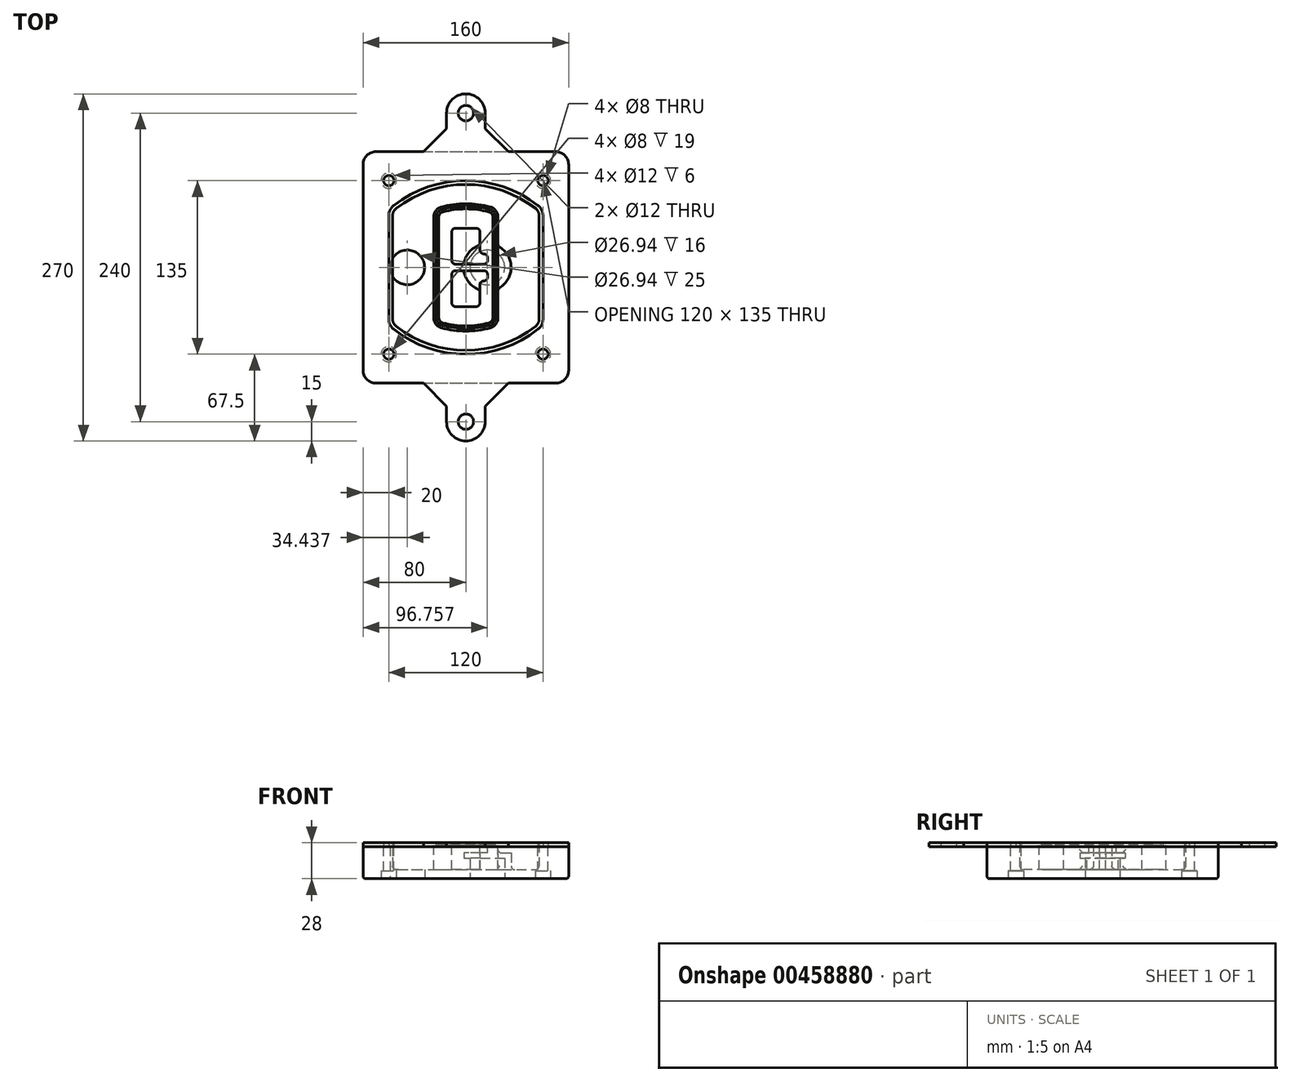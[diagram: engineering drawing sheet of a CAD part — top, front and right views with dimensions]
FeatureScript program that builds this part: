
annotation { "Feature Type Name" : "Feature", "Feature Type Description" : "" }
export const myFeature = defineFeature(function(context is Context, id is Id, definition is map)
    precondition{}
    {
        {
            var Q0;
            Q0=qCreatedBy(makeId("Top.planeOp"),FACE);
            var sketch = newSketch(context, id + "F0", { "sketchPlane" : qUnion([Q0])});
            skPoint(sketch, "E0.rect.middle", {"position": v(0, 0) * mm});
            skLineSegment(sketch, "E1.bottom", {"start": v(-70, -90) * mm, "end": v(70, -90) * mm});
            skLineSegment(sketch, "E1.top", {"start": v(-70, 90) * mm, "end": v(70, 90) * mm});
            skLineSegment(sketch, "E1.left", {"start": v(-80, -80) * mm, "end": v(-80, 80) * mm});
            skLineSegment(sketch, "E1.right", {"start": v(80, -80) * mm, "end": v(80, 80) * mm});
            skLineSegment(sketch, "E2", {"start": v(-80, 90) * mm, "end": v(80, -90) * mm, "construction": true});
            skLineSegment(sketch, "E3", {"start": v(80, 90) * mm, "end": v(-80, -90) * mm, "construction": true});
            skCircle(sketch, "E4", {"center": v(-60, 67.5) * mm, "radius": 4 * mm});
            skCircle(sketch, "E5", {"center": v(60, 67.5) * mm, "radius": 4 * mm});
            skCircle(sketch, "E6", {"center": v(60, -67.5) * mm, "radius": 4 * mm});
            skCircle(sketch, "E7", {"center": v(-60, -67.5) * mm, "radius": 4 * mm});
            skLineSegment(sketch, "E8", {"start": v(-60, 67.5) * mm, "end": v(60, 67.5) * mm, "construction": true});
            skLineSegment(sketch, "E9", {"start": v(60, 67.5) * mm, "end": v(60, -67.5) * mm, "construction": true});
            skLineSegment(sketch, "E10", {"start": v(60, -67.5) * mm, "end": v(-60, -67.5) * mm, "construction": true});
            skLineSegment(sketch, "E11", {"start": v(-60, -67.5) * mm, "end": v(-60, 67.5) * mm, "construction": true});
            skLineSegment(sketch, "E12", {"start": v(-60, 40.3) * mm, "end": v(-60, -40.3) * mm});
            skLineSegment(sketch, "E13", {"start": v(60, 40.3) * mm, "end": v(60, -40.3) * mm});
            skArc(sketch, "E14", {"start": v(56.15, 48.18) * mm, "mid": v(0, 67.5) * mm, "end": v(-56.15, 48.18) * mm});
            skArc(sketch, "E15", {"start": v(-56.15, -48.18) * mm, "mid": v(0, -67.5) * mm, "end": v(56.15, -48.18) * mm});
            skLineSegment(sketch, "E16", {"start": v(-60, 0) * mm, "end": v(60, 0) * mm, "construction": true});
            skPoint(sketch, "E17.visualSharp", {"position": v(-60, -45) * mm});
            skArc(sketch, "E17.filletArc", {"start": v(-60, -40.3) * mm, "mid": v(-58.99, -44.68) * mm, "end": v(-56.15, -48.18) * mm});
            skPoint(sketch, "E18.visualSharp", {"position": v(-60, 45) * mm});
            skArc(sketch, "E18.filletArc", {"start": v(-56.15, 48.18) * mm, "mid": v(-58.99, 44.68) * mm, "end": v(-60, 40.3) * mm});
            skPoint(sketch, "E19.visualSharp", {"position": v(60, 45) * mm});
            skArc(sketch, "E19.filletArc", {"start": v(60, 40.3) * mm, "mid": v(58.99, 44.68) * mm, "end": v(56.15, 48.18) * mm});
            skPoint(sketch, "E20.visualSharp", {"position": v(60, -45) * mm});
            skArc(sketch, "E20.filletArc", {"start": v(56.15, -48.18) * mm, "mid": v(58.99, -44.68) * mm, "end": v(60, -40.3) * mm});
            skPoint(sketch, "E21.visualSharp", {"position": v(-80, 90) * mm});
            skArc(sketch, "E21.filletArc", {"start": v(-70, 90) * mm, "mid": v(-77.07, 87.07) * mm, "end": v(-80, 80) * mm});
            skPoint(sketch, "E22.visualSharp", {"position": v(80, 90) * mm});
            skArc(sketch, "E22.filletArc", {"start": v(80, 80) * mm, "mid": v(77.07, 87.07) * mm, "end": v(70, 90) * mm});
            skPoint(sketch, "E23.visualSharp", {"position": v(80, -90) * mm});
            skArc(sketch, "E23.filletArc", {"start": v(70, -90) * mm, "mid": v(77.07, -87.07) * mm, "end": v(80, -80) * mm});
            skPoint(sketch, "E24.visualSharp", {"position": v(-80, -90) * mm});
            skArc(sketch, "E24.filletArc", {"start": v(-80, -80) * mm, "mid": v(-77.07, -87.07) * mm, "end": v(-70, -90) * mm});
            skArc(sketch, "E25.0", {"start": v(57, 40.3) * mm, "mid": v(56.3, 43.36) * mm, "end": v(54.3, 45.81) * mm});
            skLineSegment(sketch, "E25.1", {"start": v(57, 40.3) * mm, "end": v(57, -40.3) * mm});
            skArc(sketch, "E25.2", {"start": v(54.3, -45.81) * mm, "mid": v(56.3, -43.36) * mm, "end": v(57, -40.3) * mm});
            skArc(sketch, "E25.3", {"start": v(-54.3, -45.81) * mm, "mid": v(0, -64.5) * mm, "end": v(54.3, -45.81) * mm});
            skArc(sketch, "E25.4", {"start": v(-57, -40.3) * mm, "mid": v(-56.3, -43.36) * mm, "end": v(-54.3, -45.81) * mm});
            skArc(sketch, "E25.5", {"start": v(54.3, 45.81) * mm, "mid": v(0, 64.5) * mm, "end": v(-54.3, 45.81) * mm});
            skLineSegment(sketch, "E25.6", {"start": v(-57, 40.3) * mm, "end": v(-57, -40.3) * mm});
            skArc(sketch, "E25.7", {"start": v(-54.3, 45.81) * mm, "mid": v(-56.3, 43.36) * mm, "end": v(-57, 40.3) * mm});
            skArc(sketch, "E26.0", {"start": v(-58.62, 51.33) * mm, "mid": v(-62.58, 46.43) * mm, "end": v(-64, 40.3) * mm});
            skArc(sketch, "E26.1", {"start": v(58.62, 51.33) * mm, "mid": v(0, 71.5) * mm, "end": v(-58.62, 51.33) * mm});
            skArc(sketch, "E26.2", {"start": v(64, 40.3) * mm, "mid": v(62.58, 46.43) * mm, "end": v(58.62, 51.33) * mm});
            skLineSegment(sketch, "E26.3", {"start": v(64, 40.3) * mm, "end": v(64, -40.3) * mm});
            skArc(sketch, "E26.4", {"start": v(58.62, -51.33) * mm, "mid": v(62.58, -46.43) * mm, "end": v(64, -40.3) * mm});
            skLineSegment(sketch, "E26.5", {"start": v(-64, 40.3) * mm, "end": v(-64, -40.3) * mm});
            skArc(sketch, "E26.6", {"start": v(-58.62, -51.33) * mm, "mid": v(0, -71.5) * mm, "end": v(58.62, -51.33) * mm});
            skArc(sketch, "E26.7", {"start": v(-64, -40.3) * mm, "mid": v(-62.58, -46.43) * mm, "end": v(-58.62, -51.33) * mm});
            skSolve(sketch);
        }
        {
            var Q0;
            Q0=makeQuery(id+"F0.imprint","IMPRINT",FACE,{"disambiguationData":[TD([[makeQuery(id+"F0.imprint","IMPRINT",EDGE,{"derivedFrom":sQuery(id+"F0.wireOp",EDGE,"E1.bottom")}),1.0]])]});
            var Q1;
            Q1=makeQuery(id+"F0.imprint","IMPRINT",FACE,{"disambiguationData":[TD([[makeQuery(id+"F0.imprint","IMPRINT",EDGE,{"derivedFrom":sQuery(id+"F0.wireOp",EDGE,"E12")}),1.0]])]});
            var Q2;
            Q2=makeQuery(id+"F0.imprint","IMPRINT",FACE,{"disambiguationData":[TD([[makeQuery(id+"F0.imprint","IMPRINT",EDGE,{"derivedFrom":sQuery(id+"F0.wireOp",EDGE,"E25.0")}),1.0]])]});
            var Q3;
            Q3=makeQuery(id+"F0.imprint","IMPRINT",FACE,{"disambiguationData":[TD([[makeQuery(id+"F0.imprint","IMPRINT",EDGE,{"derivedFrom":sQuery(id+"F0.wireOp",EDGE,"E12")}),-1.0]])]});
            extrude(context, id + "F1", {"entities" : qUnion([Q0, Q1, Q2, Q3]), "oppositeDirection" : true, "depth" : 25 * mm});
        }
        {
            var Q0;
            Q0=makeQuery(id+"F0.imprint","IMPRINT",FACE,{"disambiguationData":[TD([[makeQuery(id+"F0.imprint","IMPRINT",EDGE,{"derivedFrom":sQuery(id+"F0.wireOp",EDGE,"E12")}),1.0]])]});
            extrude(context, id + "F2", {"entities" : qUnion([Q0]), "operationType" : NewBodyOperationType.ADD, "depth" : 3 * mm});
        }
        {
            var Q0;
            Q0=makeQuery(id+"F0.imprint","IMPRINT",FACE,{"disambiguationData":[TD([[makeQuery(id+"F0.imprint","IMPRINT",EDGE,{"derivedFrom":sQuery(id+"F0.wireOp",EDGE,"E25.0")}),1.0]])]});
            extrude(context, id + "F3", {"entities" : qUnion([Q0]), "operationType" : NewBodyOperationType.REMOVE, "oppositeDirection" : true, "depth" : 18 * mm});
        }
        {
            var Q0;
            Q0=makeQuery(id+"F2.opExtrude","CAP_FACE",FACE,{"disambiguationData":[OSD([sQuery(id+"F0.wireOp",EDGE,"E12"),sQuery(id+"F0.wireOp",EDGE,"E13"),sQuery(id+"F0.wireOp",EDGE,"E14"),sQuery(id+"F0.wireOp",EDGE,"E15"),sQuery(id+"F0.wireOp",EDGE,"E17.filletArc"),sQuery(id+"F0.wireOp",EDGE,"E18.filletArc"),sQuery(id+"F0.wireOp",EDGE,"E19.filletArc"),sQuery(id+"F0.wireOp",EDGE,"E20.filletArc"),sQuery(id+"F0.wireOp",EDGE,"E25.0"),sQuery(id+"F0.wireOp",EDGE,"E25.1"),sQuery(id+"F0.wireOp",EDGE,"E25.2"),sQuery(id+"F0.wireOp",EDGE,"E25.3"),sQuery(id+"F0.wireOp",EDGE,"E25.4"),sQuery(id+"F0.wireOp",EDGE,"E25.5"),sQuery(id+"F0.wireOp",EDGE,"E25.6"),sQuery(id+"F0.wireOp",EDGE,"E25.7")])],"isStart":false});
            var sketch = newSketch(context, id + "F4", { "sketchPlane" : qUnion([Q0])});
            skArc(sketch, "E27.0", {"start": v(-19.08, -46.97) * mm, "mid": v(0, -49.5) * mm, "end": v(19.08, -46.97) * mm});
            skArc(sketch, "E28.0", {"start": v(19.08, 46.97) * mm, "mid": v(0, 49.5) * mm, "end": v(-19.08, 46.97) * mm});
            skLineSegment(sketch, "E29", {"start": v(-25, 39.25) * mm, "end": v(-25, -39.25) * mm});
            skLineSegment(sketch, "E30", {"start": v(25, 39.25) * mm, "end": v(25, -39.25) * mm});
            skLineSegment(sketch, "E31", {"start": v(-25, 45.1) * mm, "end": v(25, 45.1) * mm, "construction": true});
            skLineSegment(sketch, "E32", {"start": v(-25, -45.1) * mm, "end": v(25, -45.1) * mm, "construction": true});
            skPoint(sketch, "E33.visualSharp", {"position": v(-25, 45.1) * mm});
            skArc(sketch, "E33.filletArc", {"start": v(-19.08, 46.97) * mm, "mid": v(-23.35, 44.11) * mm, "end": v(-25, 39.25) * mm});
            skPoint(sketch, "E34.visualSharp", {"position": v(25, 45.1) * mm});
            skArc(sketch, "E34.filletArc", {"start": v(25, 39.25) * mm, "mid": v(23.35, 44.11) * mm, "end": v(19.08, 46.97) * mm});
            skPoint(sketch, "E35.visualSharp", {"position": v(25, -45.1) * mm});
            skArc(sketch, "E35.filletArc", {"start": v(19.08, -46.97) * mm, "mid": v(23.35, -44.11) * mm, "end": v(25, -39.25) * mm});
            skPoint(sketch, "E36.visualSharp", {"position": v(-25, -45.1) * mm});
            skArc(sketch, "E36.filletArc", {"start": v(-25, -39.25) * mm, "mid": v(-23.35, -44.11) * mm, "end": v(-19.08, -46.97) * mm});
            skArc(sketch, "E37.0", {"start": v(54.3, 45.81) * mm, "mid": v(0, 64.5) * mm, "end": v(-54.3, 45.81) * mm});
            skArc(sketch, "E37.1", {"start": v(-54.3, 45.81) * mm, "mid": v(-56.3, 43.36) * mm, "end": v(-57, 40.3) * mm});
            skLineSegment(sketch, "E37.2", {"start": v(-57, 40.3) * mm, "end": v(-57, -40.3) * mm});
            skArc(sketch, "E37.3", {"start": v(-57, -40.3) * mm, "mid": v(-56.3, -43.36) * mm, "end": v(-54.3, -45.81) * mm});
            skArc(sketch, "E37.4", {"start": v(-54.3, -45.81) * mm, "mid": v(0, -64.5) * mm, "end": v(54.3, -45.81) * mm});
            skArc(sketch, "E37.5", {"start": v(54.3, -45.81) * mm, "mid": v(56.3, -43.36) * mm, "end": v(57, -40.3) * mm});
            skLineSegment(sketch, "E37.6", {"start": v(57, 40.3) * mm, "end": v(57, -40.3) * mm});
            skArc(sketch, "E37.7", {"start": v(57, 40.3) * mm, "mid": v(56.3, 43.36) * mm, "end": v(54.3, 45.81) * mm});
            skLineSegment(sketch, "E38.0", {"start": v(23, 39.25) * mm, "end": v(23, -39.25) * mm});
            skArc(sketch, "E38.1", {"start": v(18.56, -45.04) * mm, "mid": v(21.76, -42.9) * mm, "end": v(23, -39.25) * mm});
            skArc(sketch, "E38.2", {"start": v(-18.56, -45.04) * mm, "mid": v(0, -47.5) * mm, "end": v(18.56, -45.04) * mm});
            skArc(sketch, "E38.3", {"start": v(-23, -39.25) * mm, "mid": v(-21.76, -42.9) * mm, "end": v(-18.56, -45.04) * mm});
            skLineSegment(sketch, "E38.4", {"start": v(-23, 39.25) * mm, "end": v(-23, -39.25) * mm});
            skArc(sketch, "E38.5", {"start": v(23, 39.25) * mm, "mid": v(21.76, 42.9) * mm, "end": v(18.56, 45.04) * mm});
            skArc(sketch, "E38.6", {"start": v(-18.56, 45.04) * mm, "mid": v(-21.76, 42.9) * mm, "end": v(-23, 39.25) * mm});
            skArc(sketch, "E38.7", {"start": v(18.56, 45.04) * mm, "mid": v(0, 47.5) * mm, "end": v(-18.56, 45.04) * mm});
            skArc(sketch, "E39.0", {"start": v(21, 39.25) * mm, "mid": v(20.18, 41.68) * mm, "end": v(18.04, 43.1) * mm});
            skLineSegment(sketch, "E39.1", {"start": v(21, 39.25) * mm, "end": v(21, -39.25) * mm});
            skArc(sketch, "E39.2", {"start": v(18.04, -43.1) * mm, "mid": v(20.18, -41.68) * mm, "end": v(21, -39.25) * mm});
            skArc(sketch, "E39.3", {"start": v(-18.04, -43.1) * mm, "mid": v(0, -45.5) * mm, "end": v(18.04, -43.1) * mm});
            skArc(sketch, "E39.4", {"start": v(-21, -39.25) * mm, "mid": v(-20.18, -41.68) * mm, "end": v(-18.04, -43.1) * mm});
            skArc(sketch, "E39.5", {"start": v(18.04, 43.1) * mm, "mid": v(0, 45.5) * mm, "end": v(-18.04, 43.1) * mm});
            skLineSegment(sketch, "E39.6", {"start": v(-21, 39.25) * mm, "end": v(-21, -39.25) * mm});
            skArc(sketch, "E39.7", {"start": v(-18.04, 43.1) * mm, "mid": v(-20.18, 41.68) * mm, "end": v(-21, 39.25) * mm});
            skLineSegment(sketch, "E40", {"start": v(-25, 0) * mm, "end": v(25, 0) * mm, "construction": true});
            skLineSegment(sketch, "E41", {"start": v(-11, 5.5) * mm, "end": v(-11, 27.5) * mm});
            skLineSegment(sketch, "E42", {"start": v(-8, 30.5) * mm, "end": v(8, 30.5) * mm});
            skLineSegment(sketch, "E43", {"start": v(11, 27.5) * mm, "end": v(11, 13.5) * mm});
            skLineSegment(sketch, "E44", {"start": v(14, 10.5) * mm, "end": v(14, 10.5) * mm});
            skLineSegment(sketch, "E45", {"start": v(17, 7.5) * mm, "end": v(17, 5.5) * mm});
            skLineSegment(sketch, "E46", {"start": v(14, 2.5) * mm, "end": v(-8, 2.5) * mm});
            skPoint(sketch, "E47.visualSharp", {"position": v(-11, 30.5) * mm});
            skArc(sketch, "E47.filletArc", {"start": v(-8, 30.5) * mm, "mid": v(-10.12, 29.62) * mm, "end": v(-11, 27.5) * mm});
            skPoint(sketch, "E48.visualSharp", {"position": v(11, 30.5) * mm});
            skArc(sketch, "E48.filletArc", {"start": v(11, 27.5) * mm, "mid": v(10.12, 29.62) * mm, "end": v(8, 30.5) * mm});
            skPoint(sketch, "E49.visualSharp", {"position": v(11, 10.5) * mm});
            skArc(sketch, "E49.filletArc", {"start": v(11, 13.5) * mm, "mid": v(11.88, 11.38) * mm, "end": v(14, 10.5) * mm});
            skPoint(sketch, "E50.visualSharp", {"position": v(17, 10.5) * mm});
            skArc(sketch, "E50.filletArc", {"start": v(17, 7.5) * mm, "mid": v(16.12, 9.62) * mm, "end": v(14, 10.5) * mm});
            skPoint(sketch, "E51.visualSharp", {"position": v(17, 2.5) * mm});
            skArc(sketch, "E51.filletArc", {"start": v(14, 2.5) * mm, "mid": v(16.12, 3.38) * mm, "end": v(17, 5.5) * mm});
            skPoint(sketch, "E52.visualSharp", {"position": v(-11, 2.5) * mm});
            skArc(sketch, "E52.filletArc", {"start": v(-11, 5.5) * mm, "mid": v(-10.12, 3.38) * mm, "end": v(-8, 2.5) * mm});
            skLineSegment(sketch, "E53.0.MirrorCS", {"start": v(14, -2.5) * mm, "end": v(-8, -2.5) * mm});
            skArc(sketch, "E54.0.MirrorCS", {"start": v(-11, -5.5) * mm, "mid": v(-10.12, -3.38) * mm, "end": v(-8, -2.5) * mm});
            skLineSegment(sketch, "E55.0.MirrorCS", {"start": v(-11, -5.5) * mm, "end": v(-11, -27.5) * mm});
            skArc(sketch, "E56.0.MirrorCS", {"start": v(-8, -30.5) * mm, "mid": v(-10.12, -29.62) * mm, "end": v(-11, -27.5) * mm});
            skLineSegment(sketch, "E57.0.MirrorCS", {"start": v(-8, -30.5) * mm, "end": v(8, -30.5) * mm});
            skArc(sketch, "E58.0.MirrorCS", {"start": v(11, -27.5) * mm, "mid": v(10.12, -29.62) * mm, "end": v(8, -30.5) * mm});
            skLineSegment(sketch, "E59.0.MirrorCS", {"start": v(11, -27.5) * mm, "end": v(11, -13.5) * mm});
            skArc(sketch, "E60.0.MirrorCS", {"start": v(11, -13.5) * mm, "mid": v(11.88, -11.38) * mm, "end": v(14, -10.5) * mm});
            skArc(sketch, "E61.0.MirrorCS", {"start": v(17, -7.5) * mm, "mid": v(16.12, -9.62) * mm, "end": v(14, -10.5) * mm});
            skLineSegment(sketch, "E62.0.MirrorCS", {"start": v(17, -7.5) * mm, "end": v(17, -5.5) * mm});
            skArc(sketch, "E63.0.MirrorCS", {"start": v(14, -2.5) * mm, "mid": v(16.12, -3.38) * mm, "end": v(17, -5.5) * mm});
            skSolve(sketch);
        }
        {
            var Q0;
            Q0=makeQuery(id+"F4.imprint","IMPRINT",FACE,{"disambiguationData":[TD([[makeQuery(id+"F4.imprint","IMPRINT",EDGE,{"derivedFrom":sQuery(id+"F4.wireOp",EDGE,"E27.0")}),1.0]])]});
            var Q1;
            Q1=makeQuery(id+"F4.imprint","IMPRINT",FACE,{"disambiguationData":[TD([[makeQuery(id+"F4.imprint","IMPRINT",EDGE,{"derivedFrom":sQuery(id+"F4.wireOp",EDGE,"E38.0")}),-1.0]])]});
            var Q2;
            Q2=makeQuery(id+"F4.imprint","IMPRINT",FACE,{"disambiguationData":[TD([[makeQuery(id+"F4.imprint","IMPRINT",EDGE,{"derivedFrom":sQuery(id+"F4.wireOp",EDGE,"E39.0")}),1.0]])]});
            extrude(context, id + "F5", {"entities" : qUnion([Q0, Q1, Q2]), "operationType" : NewBodyOperationType.ADD, "endBound" : BoundingType.UP_TO_NEXT, "oppositeDirection" : true, "depth" : 25 * mm});
        }
        {
            var Q0;
            Q0=makeQuery(id+"F4.imprint","IMPRINT",FACE,{"disambiguationData":[TD([[makeQuery(id+"F4.imprint","IMPRINT",EDGE,{"derivedFrom":sQuery(id+"F4.wireOp",EDGE,"E38.0")}),-1.0]])]});
            extrude(context, id + "F6", {"entities" : qUnion([Q0]), "operationType" : NewBodyOperationType.REMOVE, "oppositeDirection" : true, "depth" : 2 * mm});
        }
        {
            var Q0;
            Q0=makeQuery(id+"F1.opExtrude","CAP_FACE",FACE,{"disambiguationData":[OSD([sQuery(id+"F0.wireOp",EDGE,"E1.bottom"),sQuery(id+"F0.wireOp",EDGE,"E1.top"),sQuery(id+"F0.wireOp",EDGE,"E1.left"),sQuery(id+"F0.wireOp",EDGE,"E1.right"),sQuery(id+"F0.wireOp",EDGE,"E4"),sQuery(id+"F0.wireOp",EDGE,"E5"),sQuery(id+"F0.wireOp",EDGE,"E6"),sQuery(id+"F0.wireOp",EDGE,"E7"),sQuery(id+"F0.wireOp",EDGE,"E21.filletArc"),sQuery(id+"F0.wireOp",EDGE,"E22.filletArc"),sQuery(id+"F0.wireOp",EDGE,"E23.filletArc"),sQuery(id+"F0.wireOp",EDGE,"E24.filletArc")])],"isStart":false});
            var sketch = newSketch(context, id + "F7", { "sketchPlane" : qUnion([Q0])});
            skCircle(sketch, "E64", {"center": v(16.76, 0) * mm, "radius": 13.47 * mm});
            skCircle(sketch, "E65", {"center": v(-45.56, 0) * mm, "radius": 13.47 * mm});
            skLineSegment(sketch, "E66", {"start": v(80, 0) * mm, "end": v(-80, 0) * mm});
            skCircle(sketch, "E67", {"center": v(16.76, 0) * mm, "radius": 18.47 * mm});
            skCircle(sketch, "E68", {"center": v(60, -67.5) * mm, "radius": 6 * mm});
            skCircle(sketch, "E69", {"center": v(-60, -67.5) * mm, "radius": 6 * mm});
            skCircle(sketch, "E70", {"center": v(-60, 67.5) * mm, "radius": 6 * mm});
            skCircle(sketch, "E71", {"center": v(60, 67.5) * mm, "radius": 6 * mm});
            skSolve(sketch);
        }
        {
            var Q0;
            {var subQ1=sQuery(id+"F7.wireOp",EDGE,"E66");var subQ4=sQuery(id+"F7.wireOp",EDGE,"E64");var subQ6=makeQuery(id+"F7.imprint","INTERSECT",VERTEX,{"disambiguationData":[OD(0.0)],"derivedFrom":[subQ4,subQ1]});Q0=makeQuery(id+"F7.imprint","IMPRINT",FACE,{"disambiguationData":[TD([[makeQuery(id+"F7.imprint","IMPRINT",EDGE,{"disambiguationData":[TD([[subQ6,-1.0]])],"derivedFrom":subQ4}),-1.0]])]});}
            var Q1;
            {var subQ0=sQuery(id+"F7.wireOp",EDGE,"E66");var subQ1=sQuery(id+"F7.wireOp",EDGE,"E64");var subQ3=makeQuery(id+"F7.imprint","INTERSECT",VERTEX,{"disambiguationData":[OD(0.0)],"derivedFrom":[subQ1,subQ0]});Q1=makeQuery(id+"F7.imprint","IMPRINT",FACE,{"disambiguationData":[TD([[makeQuery(id+"F7.imprint","IMPRINT",EDGE,{"disambiguationData":[TD([[subQ3,-1.0]])],"derivedFrom":subQ1}),1.0]])]});}
            var Q2;
            {var subQ0=sQuery(id+"F7.wireOp",EDGE,"E66");var subQ1=sQuery(id+"F7.wireOp",EDGE,"E64");var subQ3=makeQuery(id+"F7.imprint","INTERSECT",VERTEX,{"disambiguationData":[OD(0.0)],"derivedFrom":[subQ1,subQ0]});Q2=makeQuery(id+"F7.imprint","IMPRINT",FACE,{"disambiguationData":[TD([[makeQuery(id+"F7.imprint","IMPRINT",EDGE,{"disambiguationData":[TD([[subQ3,1.0]])],"derivedFrom":subQ1}),1.0]])]});}
            var Q3;
            {var subQ1=sQuery(id+"F7.wireOp",EDGE,"E66");var subQ4=sQuery(id+"F7.wireOp",EDGE,"E64");var subQ6=makeQuery(id+"F7.imprint","INTERSECT",VERTEX,{"disambiguationData":[OD(0.0)],"derivedFrom":[subQ4,subQ1]});Q3=makeQuery(id+"F7.imprint","IMPRINT",FACE,{"disambiguationData":[TD([[makeQuery(id+"F7.imprint","IMPRINT",EDGE,{"disambiguationData":[TD([[subQ6,1.0]])],"derivedFrom":subQ4}),-1.0]])]});}
            extrude(context, id + "F8", {"entities" : qUnion([Q0, Q1, Q2, Q3]), "operationType" : NewBodyOperationType.ADD, "oppositeDirection" : true, "depth" : 20 * mm});
        }
        {
            var Q0;
            {var subQ0=sQuery(id+"F7.wireOp",EDGE,"E66");var subQ1=sQuery(id+"F7.wireOp",EDGE,"E64");var subQ3=makeQuery(id+"F7.imprint","INTERSECT",VERTEX,{"disambiguationData":[OD(0.0)],"derivedFrom":[subQ1,subQ0]});Q0=makeQuery(id+"F7.imprint","IMPRINT",FACE,{"disambiguationData":[TD([[makeQuery(id+"F7.imprint","IMPRINT",EDGE,{"disambiguationData":[TD([[subQ3,-1.0]])],"derivedFrom":subQ1}),1.0]])]});}
            var Q1;
            {var subQ0=sQuery(id+"F7.wireOp",EDGE,"E66");var subQ1=sQuery(id+"F7.wireOp",EDGE,"E64");var subQ3=makeQuery(id+"F7.imprint","INTERSECT",VERTEX,{"disambiguationData":[OD(0.0)],"derivedFrom":[subQ1,subQ0]});Q1=makeQuery(id+"F7.imprint","IMPRINT",FACE,{"disambiguationData":[TD([[makeQuery(id+"F7.imprint","IMPRINT",EDGE,{"disambiguationData":[TD([[subQ3,1.0]])],"derivedFrom":subQ1}),1.0]])]});}
            extrude(context, id + "F9", {"entities" : qUnion([Q0, Q1]), "operationType" : NewBodyOperationType.REMOVE, "oppositeDirection" : true, "depth" : 16 * mm});
        }
        {
            var Q0;
            {var subQ0=sQuery(id+"F7.wireOp",EDGE,"E66");var subQ1=sQuery(id+"F7.wireOp",EDGE,"E65");var subQ3=makeQuery(id+"F7.imprint","INTERSECT",VERTEX,{"disambiguationData":[OD(0.0)],"derivedFrom":[subQ1,subQ0]});Q0=makeQuery(id+"F7.imprint","IMPRINT",FACE,{"disambiguationData":[TD([[makeQuery(id+"F7.imprint","IMPRINT",EDGE,{"disambiguationData":[TD([[subQ3,-1.0]])],"derivedFrom":subQ1}),1.0]])]});}
            var Q1;
            {var subQ0=sQuery(id+"F7.wireOp",EDGE,"E66");var subQ1=sQuery(id+"F7.wireOp",EDGE,"E65");var subQ3=makeQuery(id+"F7.imprint","INTERSECT",VERTEX,{"disambiguationData":[OD(0.0)],"derivedFrom":[subQ1,subQ0]});Q1=makeQuery(id+"F7.imprint","IMPRINT",FACE,{"disambiguationData":[TD([[makeQuery(id+"F7.imprint","IMPRINT",EDGE,{"disambiguationData":[TD([[subQ3,1.0]])],"derivedFrom":subQ1}),1.0]])]});}
            extrude(context, id + "F10", {"entities" : qUnion([Q0, Q1]), "operationType" : NewBodyOperationType.REMOVE, "oppositeDirection" : true, "depth" : 25 * mm});
        }
        {
            var Q0;
            Q0=makeQuery(id+"F7.imprint","IMPRINT",FACE,{"disambiguationData":[TD([[makeQuery(id+"F7.imprint","IMPRINT",EDGE,{"derivedFrom":sQuery(id+"F7.wireOp",EDGE,"E68")}),1.0]])]});
            var Q1;
            Q1=makeQuery(id+"F7.imprint","IMPRINT",FACE,{"disambiguationData":[TD([[makeQuery(id+"F7.imprint","IMPRINT",EDGE,{"derivedFrom":makeQuery(id+"F1.opExtrude","CAP_EDGE",EDGE,{"disambiguationData":[OSD([sQuery(id+"F0.wireOp",EDGE,"E5")])],"isStart":false})}),-1.0]])]});
            var Q2;
            Q2=makeQuery(id+"F7.imprint","IMPRINT",FACE,{"disambiguationData":[TD([[makeQuery(id+"F7.imprint","IMPRINT",EDGE,{"derivedFrom":sQuery(id+"F7.wireOp",EDGE,"E69")}),1.0]])]});
            var Q3;
            Q3=makeQuery(id+"F7.imprint","IMPRINT",FACE,{"disambiguationData":[TD([[makeQuery(id+"F7.imprint","IMPRINT",EDGE,{"derivedFrom":makeQuery(id+"F1.opExtrude","CAP_EDGE",EDGE,{"disambiguationData":[OSD([sQuery(id+"F0.wireOp",EDGE,"E4")])],"isStart":false})}),-1.0]])]});
            var Q4;
            Q4=makeQuery(id+"F7.imprint","IMPRINT",FACE,{"disambiguationData":[TD([[makeQuery(id+"F7.imprint","IMPRINT",EDGE,{"derivedFrom":sQuery(id+"F7.wireOp",EDGE,"E70")}),1.0]])]});
            var Q5;
            Q5=makeQuery(id+"F7.imprint","IMPRINT",FACE,{"disambiguationData":[TD([[makeQuery(id+"F7.imprint","IMPRINT",EDGE,{"derivedFrom":makeQuery(id+"F1.opExtrude","CAP_EDGE",EDGE,{"disambiguationData":[OSD([sQuery(id+"F0.wireOp",EDGE,"E7")])],"isStart":false})}),-1.0]])]});
            var Q6;
            Q6=makeQuery(id+"F7.imprint","IMPRINT",FACE,{"disambiguationData":[TD([[makeQuery(id+"F7.imprint","IMPRINT",EDGE,{"derivedFrom":sQuery(id+"F7.wireOp",EDGE,"E71")}),1.0]])]});
            var Q7;
            Q7=makeQuery(id+"F7.imprint","IMPRINT",FACE,{"disambiguationData":[TD([[makeQuery(id+"F7.imprint","IMPRINT",EDGE,{"derivedFrom":makeQuery(id+"F1.opExtrude","CAP_EDGE",EDGE,{"disambiguationData":[OSD([sQuery(id+"F0.wireOp",EDGE,"E6")])],"isStart":false})}),-1.0]])]});
            extrude(context, id + "F11", {"entities" : qUnion([Q0, Q1, Q2, Q3, Q4, Q5, Q6, Q7]), "operationType" : NewBodyOperationType.REMOVE, "oppositeDirection" : true, "depth" : 6 * mm});
        }
        {
            var Q0;
            Q0=makeQuery(id+"F9.boolean.opBoolean","COPY",FACE,{"derivedFrom":makeQuery(id+"F9.opExtrude","CAP_FACE",FACE,{"disambiguationData":[OSD([sQuery(id+"F7.wireOp",EDGE,"E64")])],"isStart":false})});
            var sketch = newSketch(context, id + "F12", { "sketchPlane" : qUnion([Q0])});
            skArc(sketch, "E72.0", {"start": v(11, 17.55) * mm, "mid": v(2.57, 11.82) * mm, "end": v(-1.54, 2.5) * mm});
            skArc(sketch, "E72.1", {"start": v(-1.54, -2.5) * mm, "mid": v(2.57, -11.82) * mm, "end": v(11, -17.55) * mm});
            skLineSegment(sketch, "E73", {"start": v(-1.54, -2.5) * mm, "end": v(14, -2.5) * mm});
            skLineSegment(sketch, "E74.0", {"start": v(14, 2.5) * mm, "end": v(-1.54, 2.5) * mm});
            skArc(sketch, "E74.1", {"start": v(14, 2.5) * mm, "mid": v(16.12, 3.38) * mm, "end": v(17, 5.5) * mm});
            skLineSegment(sketch, "E74.2", {"start": v(17, 7.5) * mm, "end": v(17, 5.5) * mm});
            skArc(sketch, "E74.3", {"start": v(17, 7.5) * mm, "mid": v(16.12, 9.62) * mm, "end": v(14, 10.5) * mm});
            skArc(sketch, "E74.4", {"start": v(11, 13.5) * mm, "mid": v(11.88, 11.38) * mm, "end": v(14, 10.5) * mm});
            skLineSegment(sketch, "E74.5", {"start": v(11, 17.55) * mm, "end": v(11, 13.5) * mm});
            skLineSegment(sketch, "E74.7", {"start": v(14, -2.5) * mm, "end": v(-1.54, -2.5) * mm});
            skArc(sketch, "E74.8", {"start": v(14, -2.5) * mm, "mid": v(16.12, -3.38) * mm, "end": v(17, -5.5) * mm});
            skLineSegment(sketch, "E74.9", {"start": v(17, -7.5) * mm, "end": v(17, -5.5) * mm});
            skArc(sketch, "E74.10", {"start": v(17, -7.5) * mm, "mid": v(16.12, -9.62) * mm, "end": v(14, -10.5) * mm});
            skArc(sketch, "E74.11", {"start": v(11, -13.5) * mm, "mid": v(11.88, -11.38) * mm, "end": v(14, -10.5) * mm});
            skLineSegment(sketch, "E74.12", {"start": v(11, -17.55) * mm, "end": v(11, -13.5) * mm});
            skPoint(sketch, "E75.orphan", {"position": v(11, -27.5) * mm});
            skPoint(sketch, "E76.orphan", {"position": v(-8, -2.5) * mm});
            skPoint(sketch, "E77.orphan", {"position": v(-8, 2.5) * mm});
            skPoint(sketch, "E78.orphan", {"position": v(11, 27.5) * mm});
            skSolve(sketch);
        }
        {
            var Q0;
            {var subQ7=sQuery(id+"F12.wireOp",EDGE,"E72.0");var subQ14=sQuery(id+"F12.wireOp",EDGE,"E72.1");var subQ16=sQuery(id+"F12.wireOp",EDGE,"E74.1");var subQ18=sQuery(id+"F12.wireOp",EDGE,"E74.8");Q0=qUnion([makeQuery(id+"F12.imprint","IMPRINT",FACE,{"disambiguationData":[TD([[makeQuery(id+"F12.imprint","IMPRINT",EDGE,{"derivedFrom":subQ7}),1.0]])]}),makeQuery(id+"F12.imprint","IMPRINT",FACE,{"disambiguationData":[TD([[makeQuery(id+"F12.imprint","IMPRINT",EDGE,{"derivedFrom":subQ14}),1.0]])]}),makeQuery(id+"F12.imprint","IMPRINT",FACE,{"disambiguationData":[TD([[makeQuery(id+"F12.imprint","IMPRINT",EDGE,{"derivedFrom":subQ16}),1.0]])]}),makeQuery(id+"F12.imprint","IMPRINT",FACE,{"disambiguationData":[TD([[makeQuery(id+"F12.imprint","IMPRINT",EDGE,{"derivedFrom":subQ18}),-1.0]])]})]);}
            var Q1;
            Q1=makeQuery(id+"F5.boolean.opBoolean","SPLIT",FACE,{"disambiguationData":[TD([makeQuery(id+"F5.opExtrude","SWEPT_FACE",FACE,{"disambiguationData":[OSD([sQuery(id+"F4.wireOp",EDGE,"E41")])]})])],"derivedFrom":makeQuery(id+"F3.boolean.opBoolean","COPY",FACE,{"derivedFrom":makeQuery(id+"F3.opExtrude","CAP_FACE",FACE,{"disambiguationData":[OSD([sQuery(id+"F0.wireOp",EDGE,"E25.0"),sQuery(id+"F0.wireOp",EDGE,"E25.1"),sQuery(id+"F0.wireOp",EDGE,"E25.2"),sQuery(id+"F0.wireOp",EDGE,"E25.3"),sQuery(id+"F0.wireOp",EDGE,"E25.4"),sQuery(id+"F0.wireOp",EDGE,"E25.5"),sQuery(id+"F0.wireOp",EDGE,"E25.6"),sQuery(id+"F0.wireOp",EDGE,"E25.7")])],"isStart":false})})});
            extrude(context, id + "F13", {"entities" : qUnion([Q0]), "operationType" : NewBodyOperationType.REMOVE, "endBound" : BoundingType.UP_TO_SURFACE, "endBoundEntityFace" : qUnion([Q1]), "depth" : 25 * mm});
        }
        {
            var Q0;
            Q0=makeQuery(id+"F3.boolean.opBoolean","COPY",EDGE,{"derivedFrom":makeQuery(id+"F3.opExtrude","CAP_EDGE",EDGE,{"disambiguationData":[OSD([sQuery(id+"F0.wireOp",EDGE,"E25.6")])],"isStart":false})});
            var Q1;
            Q1=makeQuery(id+"F8.boolean.opBoolean","INTERSECT",EDGE,{"derivedFrom":[makeQuery(id+"F5.opExtrude","SWEPT_FACE",FACE,{"disambiguationData":[OSD([sQuery(id+"F4.wireOp",EDGE,"E30")])]}),makeQuery(id+"F8.opExtrude","CAP_FACE",FACE,{"disambiguationData":[OSD([sQuery(id+"F7.wireOp",EDGE,"E67")])],"isStart":false})]});
            var Q2;
            Q2=makeQuery(id+"F8.boolean.opBoolean","INTERSECT",EDGE,{"disambiguationData":[OD(1.0)],"derivedFrom":[makeQuery(id+"F5.opExtrude","SWEPT_FACE",FACE,{"disambiguationData":[OSD([sQuery(id+"F4.wireOp",EDGE,"E30")])]}),makeQuery(id+"F8.opExtrude","SWEPT_FACE",FACE,{"disambiguationData":[OSD([sQuery(id+"F7.wireOp",EDGE,"E67")])]})]});
            var Q3;
            {var subQ0=makeQuery(id+"F3.boolean.opBoolean","COPY",FACE,{"derivedFrom":makeQuery(id+"F3.opExtrude","CAP_FACE",FACE,{"disambiguationData":[OSD([sQuery(id+"F0.wireOp",EDGE,"E25.0"),sQuery(id+"F0.wireOp",EDGE,"E25.1"),sQuery(id+"F0.wireOp",EDGE,"E25.2"),sQuery(id+"F0.wireOp",EDGE,"E25.3"),sQuery(id+"F0.wireOp",EDGE,"E25.4"),sQuery(id+"F0.wireOp",EDGE,"E25.5"),sQuery(id+"F0.wireOp",EDGE,"E25.6"),sQuery(id+"F0.wireOp",EDGE,"E25.7")])],"isStart":false})});var subQ1=sQuery(id+"F4.wireOp",EDGE,"E30");Q3=makeQuery(id+"F8.boolean.opBoolean","SPLIT",EDGE,{"disambiguationData":[TD([makeQuery(id+"F5.opExtrude","SWEPT_FACE",FACE,{"disambiguationData":[OSD([sQuery(id+"F4.wireOp",EDGE,"E35.filletArc")])]})])],"derivedFrom":makeQuery(id+"F5.opExtrude","TWEAK_EDGE",EDGE,{"derivedFrom":[subQ0,makeQuery(id+"F4.imprint","IMPRINT",EDGE,{"derivedFrom":subQ1})]})});}
            var Q4;
            {var subQ0=sQuery(id+"F0.wireOp",EDGE,"E25.0");var subQ1=sQuery(id+"F0.wireOp",EDGE,"E25.1");var subQ2=sQuery(id+"F0.wireOp",EDGE,"E25.2");var subQ3=sQuery(id+"F0.wireOp",EDGE,"E25.3");var subQ4=sQuery(id+"F0.wireOp",EDGE,"E25.4");var subQ5=sQuery(id+"F0.wireOp",EDGE,"E25.5");var subQ6=sQuery(id+"F0.wireOp",EDGE,"E25.6");var subQ7=sQuery(id+"F0.wireOp",EDGE,"E25.7");Q4=makeQuery(id+"F8.boolean.opBoolean","INTERSECT",EDGE,{"derivedFrom":[makeQuery(id+"F5.boolean.opBoolean","SPLIT",FACE,{"disambiguationData":[TD([makeQuery(id+"F2.opExtrude","SWEPT_FACE",FACE,{"disambiguationData":[OSD([subQ0])]})])],"derivedFrom":makeQuery(id+"F3.boolean.opBoolean","COPY",FACE,{"derivedFrom":makeQuery(id+"F3.opExtrude","CAP_FACE",FACE,{"disambiguationData":[OSD([subQ0,subQ1,subQ2,subQ3,subQ4,subQ5,subQ6,subQ7])],"isStart":false})})}),makeQuery(id+"F8.opExtrude","SWEPT_FACE",FACE,{"disambiguationData":[OSD([sQuery(id+"F7.wireOp",EDGE,"E67")])]})]});}
            var Q5;
            Q5=makeQuery(id+"F8.boolean.opBoolean","INTERSECT",EDGE,{"disambiguationData":[OD(0.0)],"derivedFrom":[makeQuery(id+"F5.opExtrude","SWEPT_FACE",FACE,{"disambiguationData":[OSD([sQuery(id+"F4.wireOp",EDGE,"E30")])]}),makeQuery(id+"F8.opExtrude","SWEPT_FACE",FACE,{"disambiguationData":[OSD([sQuery(id+"F7.wireOp",EDGE,"E67")])]})]});
            fillet(context, id + "F14", {"entities" : qUnion([Q0, Q1, Q2, Q3, Q4, Q5]), "radius" : 3 * mm, "tangentPropagation" : true, "allowEdgeOverflow" : false});
        }
        {
            var Q0;
            Q0=makeQuery(id+"F1.opExtrude","CAP_EDGE",EDGE,{"disambiguationData":[OSD([sQuery(id+"F0.wireOp",EDGE,"E1.bottom")])],"isStart":false});
            fillet(context, id + "F15", {"entities" : qUnion([Q0]), "radius" : 2 * mm, "tangentPropagation" : true, "allowEdgeOverflow" : false});
        }
        {
            var Q0;
            {var subQ0=sQuery(id+"F0.wireOp",EDGE,"E21.filletArc");var subQ1=sQuery(id+"F0.wireOp",EDGE,"E7");var subQ2=sQuery(id+"F0.wireOp",EDGE,"E6");var subQ3=sQuery(id+"F0.wireOp",EDGE,"E5");var subQ4=sQuery(id+"F0.wireOp",EDGE,"E4");var subQ5=sQuery(id+"F0.wireOp",EDGE,"E22.filletArc");var subQ6=sQuery(id+"F0.wireOp",EDGE,"E1.bottom");var subQ7=sQuery(id+"F0.wireOp",EDGE,"E1.right");var subQ8=sQuery(id+"F0.wireOp",EDGE,"E1.top");var subQ9=sQuery(id+"F0.wireOp",EDGE,"E1.left");var subQ10=sQuery(id+"F0.wireOp",EDGE,"E23.filletArc");var subQ11=sQuery(id+"F0.wireOp",EDGE,"E24.filletArc");Q0=makeQuery(id+"F2.boolean.opBoolean","SPLIT",FACE,{"disambiguationData":[TD([makeQuery(id+"F1.opExtrude","SWEPT_FACE",FACE,{"disambiguationData":[OSD([subQ6])]})])],"derivedFrom":makeQuery(id+"F1.opExtrude","CAP_FACE",FACE,{"disambiguationData":[OSD([subQ6,subQ8,subQ9,subQ7,subQ4,subQ3,subQ2,subQ1,subQ0,subQ5,subQ10,subQ11])],"isStart":true})});}
            var sketch = newSketch(context, id + "F16", { "sketchPlane" : qUnion([Q0])});
            skLineSegment(sketch, "E79.0", {"start": v(-70, 90) * mm, "end": v(70, 90) * mm});
            skArc(sketch, "E79.1", {"start": v(-70, 90) * mm, "mid": v(-77.07, 87.07) * mm, "end": v(-80, 80) * mm});
            skLineSegment(sketch, "E79.2", {"start": v(-80, -80) * mm, "end": v(-80, 80) * mm});
            skArc(sketch, "E79.3", {"start": v(-80, -80) * mm, "mid": v(-77.07, -87.07) * mm, "end": v(-70, -90) * mm});
            skLineSegment(sketch, "E79.4", {"start": v(-70, -90) * mm, "end": v(70, -90) * mm});
            skArc(sketch, "E79.5", {"start": v(70, -90) * mm, "mid": v(77.07, -87.07) * mm, "end": v(80, -80) * mm});
            skLineSegment(sketch, "E79.6", {"start": v(80, -80) * mm, "end": v(80, 80) * mm});
            skArc(sketch, "E79.7", {"start": v(80, 80) * mm, "mid": v(77.07, 87.07) * mm, "end": v(70, 90) * mm});
            skCircle(sketch, "E79.8", {"center": v(60, 67.5) * mm, "radius": 4 * mm});
            skCircle(sketch, "E79.9", {"center": v(-60, 67.5) * mm, "radius": 4 * mm});
            skCircle(sketch, "E79.10", {"center": v(-60, -67.5) * mm, "radius": 4 * mm});
            skCircle(sketch, "E79.11", {"center": v(60, -67.5) * mm, "radius": 4 * mm});
            skArc(sketch, "E79.12", {"start": v(56.15, 48.18) * mm, "mid": v(0, 67.5) * mm, "end": v(-56.15, 48.18) * mm});
            skArc(sketch, "E79.13", {"start": v(60, 40.3) * mm, "mid": v(58.99, 44.68) * mm, "end": v(56.15, 48.18) * mm});
            skLineSegment(sketch, "E79.14", {"start": v(60, 40.3) * mm, "end": v(60, -40.3) * mm});
            skArc(sketch, "E79.15", {"start": v(56.15, -48.18) * mm, "mid": v(58.99, -44.68) * mm, "end": v(60, -40.3) * mm});
            skArc(sketch, "E79.16", {"start": v(-56.15, -48.18) * mm, "mid": v(0, -67.5) * mm, "end": v(56.15, -48.18) * mm});
            skArc(sketch, "E79.17", {"start": v(-60, -40.3) * mm, "mid": v(-58.99, -44.68) * mm, "end": v(-56.15, -48.18) * mm});
            skLineSegment(sketch, "E79.18", {"start": v(-60, 40.3) * mm, "end": v(-60, -40.3) * mm});
            skArc(sketch, "E79.19", {"start": v(-56.15, 48.18) * mm, "mid": v(-58.99, 44.68) * mm, "end": v(-60, 40.3) * mm});
            skPoint(sketch, "E79.20", {"position": v(-77.07, -87.07) * mm});
            skLineSegment(sketch, "E80", {"start": v(0, 90) * mm, "end": v(0, 120) * mm, "construction": true});
            skPoint(sketch, "E80.endSnap0", {"position": v(0, 90) * mm});
            skCircle(sketch, "E81", {"center": v(0, 120) * mm, "radius": 6 * mm});
            skArc(sketch, "E82", {"start": v(15, 120) * mm, "mid": v(0, 135) * mm, "end": v(-15, 120) * mm});
            skLineSegment(sketch, "E83", {"start": v(15, 120) * mm, "end": v(15, 108) * mm});
            skLineSegment(sketch, "E84", {"start": v(33, 90) * mm, "end": v(15, 108) * mm});
            skLineSegment(sketch, "E85.MirrorCS", {"start": v(-15, 120) * mm, "end": v(-15, 108) * mm});
            skLineSegment(sketch, "E86.MirrorCS", {"start": v(-33, 90) * mm, "end": v(-15, 108) * mm});
            skLineSegment(sketch, "E87", {"start": v(-80, 0) * mm, "end": v(80, 0) * mm, "construction": true});
            skLineSegment(sketch, "E88.MirrorCS", {"start": v(-33, -90) * mm, "end": v(-15, -108) * mm});
            skLineSegment(sketch, "E89.MirrorCS", {"start": v(-15, -120) * mm, "end": v(-15, -108) * mm});
            skLineSegment(sketch, "E90.MirrorCS", {"start": v(0, -90) * mm, "end": v(0, -120) * mm, "construction": true});
            skCircle(sketch, "E91.MirrorC", {"center": v(0, -120) * mm, "radius": 6 * mm});
            skArc(sketch, "E92.MirrorCS", {"start": v(15, -120) * mm, "mid": v(0, -135) * mm, "end": v(-15, -120) * mm});
            skLineSegment(sketch, "E93.MirrorCS", {"start": v(15, -120) * mm, "end": v(15, -108) * mm});
            skLineSegment(sketch, "E94.MirrorCS", {"start": v(33, -90) * mm, "end": v(15, -108) * mm});
            skSolve(sketch);
        }
        {
            var Q0;
            Q0 = qSketchRegion(id + "F16", true);
            var Q1;
            Q1=makeQuery(id+"F2.opExtrude","CAP_FACE",FACE,{"disambiguationData":[OSD([sQuery(id+"F0.wireOp",EDGE,"E12"),sQuery(id+"F0.wireOp",EDGE,"E13"),sQuery(id+"F0.wireOp",EDGE,"E14"),sQuery(id+"F0.wireOp",EDGE,"E15"),sQuery(id+"F0.wireOp",EDGE,"E17.filletArc"),sQuery(id+"F0.wireOp",EDGE,"E18.filletArc"),sQuery(id+"F0.wireOp",EDGE,"E19.filletArc"),sQuery(id+"F0.wireOp",EDGE,"E20.filletArc"),sQuery(id+"F0.wireOp",EDGE,"E25.0"),sQuery(id+"F0.wireOp",EDGE,"E25.1"),sQuery(id+"F0.wireOp",EDGE,"E25.2"),sQuery(id+"F0.wireOp",EDGE,"E25.3"),sQuery(id+"F0.wireOp",EDGE,"E25.4"),sQuery(id+"F0.wireOp",EDGE,"E25.5"),sQuery(id+"F0.wireOp",EDGE,"E25.6"),sQuery(id+"F0.wireOp",EDGE,"E25.7")])],"isStart":false});
            extrude(context, id + "F17", {"entities" : qUnion([Q0]), "endBound" : BoundingType.UP_TO_SURFACE, "endBoundEntityFace" : qUnion([Q1]), "depth" : 25 * mm});
        }
    });
